# Revit family: IS_Connect_E5047_BIM_DE
name_source: partatom
category: Plumbing Fixtures
revit_build: Autodesk Revit MEP 2016 (Build: 20161004_0715(x64)
units: mm (PartAtom-declared; Revit-internal decimal feet)

## family parameters
Cut with Voids When Loaded = Yes
Host = Face
OmniClass Number = 23.45.05.14.14
OmniClass Title = Sinks/Lavatories
Part Type = Normal
Room Calculation Point = No
Round Connector Dimension = Use Diameter
Shared = Yes

## types (2) — shared parameters
Accessories = www.idealstandard.de\ersatzteile
AreaUnits = millimeters
Assembly Code = C1030200
AssetType = Fixed
BIMObjectName = ISI_IdealStandard_Sinks_CONNECT_E504801
BIMobject category = Basins
Brand url = http://www.idealstandard.co.uk
CodePerformance = DIN EN 14688 CL 15, DIN EN 31
Color = White
ConnectionType = Plumbing
CurrencyUnit = €
Date of publishing = 6/23/2017
Default Elevation = 864 mm  [stored 2.83465 ft]
Description = CONNECT countertop washbasin 550x380mm, no taphole, with overflow
DurationUnit = year
Edition number = 1
ExpectedLife = 25
Features = CONNECT under countertop washbasin 550x380mm, no taphole, with overflow
Finish = White
GrossWeight = 8 kg
IFC Classification = Sanitary Terminal
Installation instructions = http://www.idealstandard.de
InstallationDate = 1900-12-31T23:59:59
InstallationInstructions = www.idealstandard.de\produkte
LinearUnits = millimeters
Manufacturer name = Ideal Standard
ManufacturerURL = www.idealstandard.de
Material = Vitreous china
Material main = Ceramics
ModelNumber = E504801
ModelReference = IS Unterbauwaschtisch CONNECT, oval, o.Hl., m.Ül., 550x380x175mm, Weiß
NBS Reference Code = 35-79-18
NBS Reference Description = Counter Top Wash Basins
Name = ISI_IdealStandard_Sinks_CONNECT_E504801
Nominal height = 175 mm
Nominal width = 550 mm
NominalLength = 380 mm
OmniClass Code = 23-31 13 00
OmniClass Description = Sinks
Product Guid = a9917935-62b5-447b-b96e-2d8f04567e46
Product SKU = E5047
Product data url = https://bimobject.com
Product family = CONNECT
Product group = Basin
Product url = http://www.idealstandard.de
ProductInformation = www.idealstandard.de
QR code = http://bimobject.com
Shape = Sculptured
Size = 550 x 380 x 175 mm
Space = Internal
Technical description = http://www.idealstandard.de
URL = www.idealstandard.de
Uniclass 1.4 Code = L7212
Uniclass 1.4 Description = Washbasins
Uniclass 2.0 Code = PR-35-79-94
Uniclass 2.0 Description = Wall-Hung Wash Basins
Uniclass 2015 Code = Pr_40_20_96_96
Uniclass 2015 Name = Wall-hung wash basins
Uniclass2015Code = Pr_40_20_96_18
Uniclass2015Title = Counter top wash basins
Uniclass2015Version = Products v1.1
Version = 1
VolumeUnits = Litres
WasteCover = ISI_IdealStandard_BasinMaterial_White3_Render
Weight Net (Kg) = 6.75
zero-valued in all types: CWFU, Cost, HWFU, NominalDepth, WFU

## per-type parameters (varying)
| type | BarCode | EAN code | Model |
| E504701 CONNECT countertop washbasin 550x380mm, no taphole, with overflow | 5017830446897 | https://5017830446897 | E504801 |
| E5047MA CONNECT countertop washbasin 550x380mm, no taphole, with overflow | 5017830446903 | https://5017830446903 | E5048MA |

note: [stored X ft] marks values corroborated as IEEE doubles in the binary element streams (Revit-internal decimal feet)

## geometry (parser evidence)
native form markers: Blend x8, Sweep x2
no freeform markers — native parametric forms only
